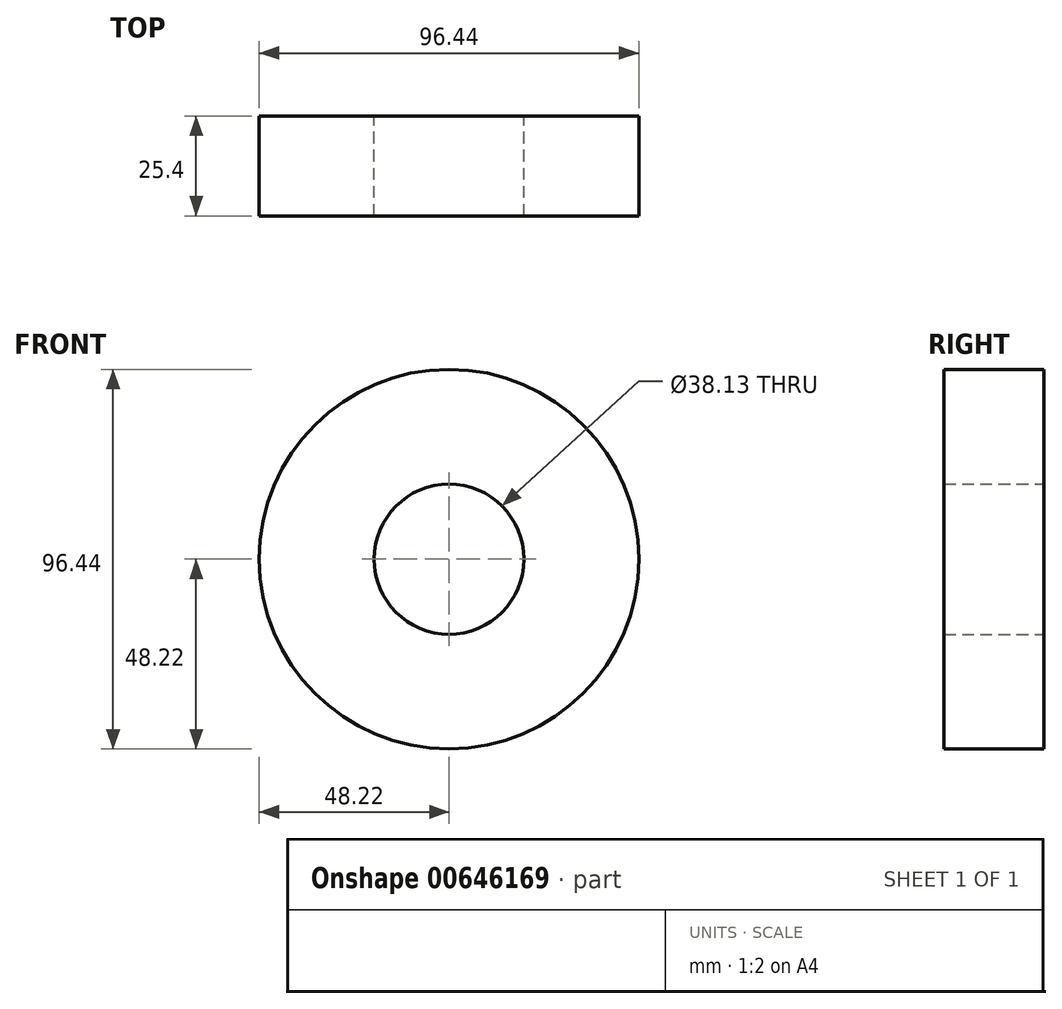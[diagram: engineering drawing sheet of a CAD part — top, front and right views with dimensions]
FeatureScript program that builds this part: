
annotation { "Feature Type Name" : "Feature", "Feature Type Description" : "" }
export const myFeature = defineFeature(function(context is Context, id is Id, definition is map)
    precondition{}
    {
        {
            var Q0;
            Q0=qCreatedBy(makeId("Front.planeOp"),FACE);
            var sketch = newSketch(context, id + "F0", { "sketchPlane" : qUnion([Q0])});
            skCircle(sketch, "E0", {"center": v(0, 0) * mm, "radius": 48.22 * mm});
            skCircle(sketch, "E1", {"center": v(0, 0) * mm, "radius": 19.07 * mm});
            skSolve(sketch);
        }
        {
            var Q0;
            Q0=makeQuery(id+"F0.imprint","IMPRINT",FACE,{"disambiguationData":[TD([[makeQuery(id+"F0.imprint","IMPRINT",EDGE,{"derivedFrom":sQuery(id+"F0.wireOp",EDGE,"E0")}),1.0]])]});
            extrude(context, id + "F1", {"entities" : qUnion([Q0]), "endBound" : BoundingType.SYMMETRIC, "depth" : 25.4 * mm, "offsetDistance" : 25.4 * mm});
        }
    });
